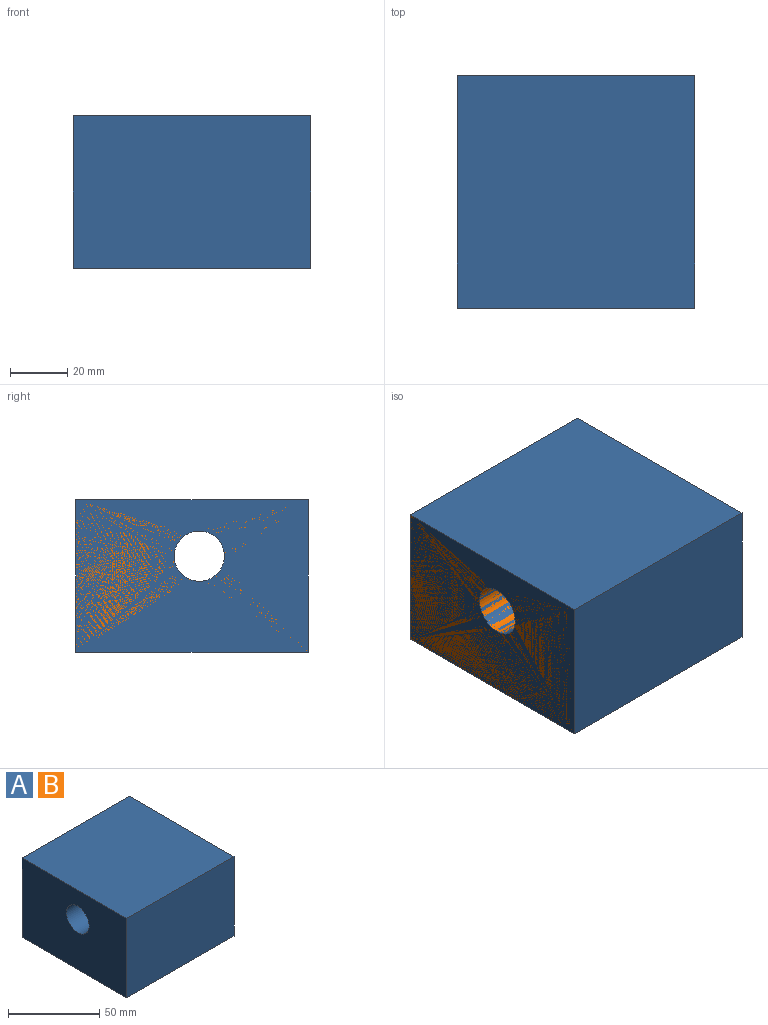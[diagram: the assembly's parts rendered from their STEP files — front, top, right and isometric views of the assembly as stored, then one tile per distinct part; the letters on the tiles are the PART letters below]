
ASSEMBLY  parts=2 mates=1
PART A: 7 faces, bbox 82.8x81.1x53.1 mm
  f0: plane 82.76x53.09mm, normal (0,1,0), area 4393.1mm2, adj f1,f3,f4,f5
  f1: plane 81.13x53.09mm, normal (-1,0,0), area 4065.4mm2, adj f0,f2,f4,f5,f6
  f2: plane 82.76x53.09mm, normal (0,-1,0), area 4393.1mm2, adj f1,f3,f4,f5
  f3: plane 81.13x53.09mm, normal (1,0,0), area 4065.4mm2, adj f0,f2,f4,f5,f6
  f4: plane 82.76x81.13mm, normal (0,0,1), area 6713.8mm2, adj f0,f1,f2,f3
  f5: plane 82.76x81.13mm, normal (0,0,-1), area 6713.8mm2, adj f0,f1,f2,f3
  f6: cylinder r=8.77mm len=82.76mm, axis (1,0,0), area 4558.1mm2, adj f1,f3
PART B: same geometry as A
PLACE A t=(1.76,3.36,17.66)mm
PLACE B t=(1.76,3.36,17.66)mm fixed
MATE fastened A.f2 <-> B.f2  axis (0,-1,0) through (5.02,-34.66,44.2)mm
